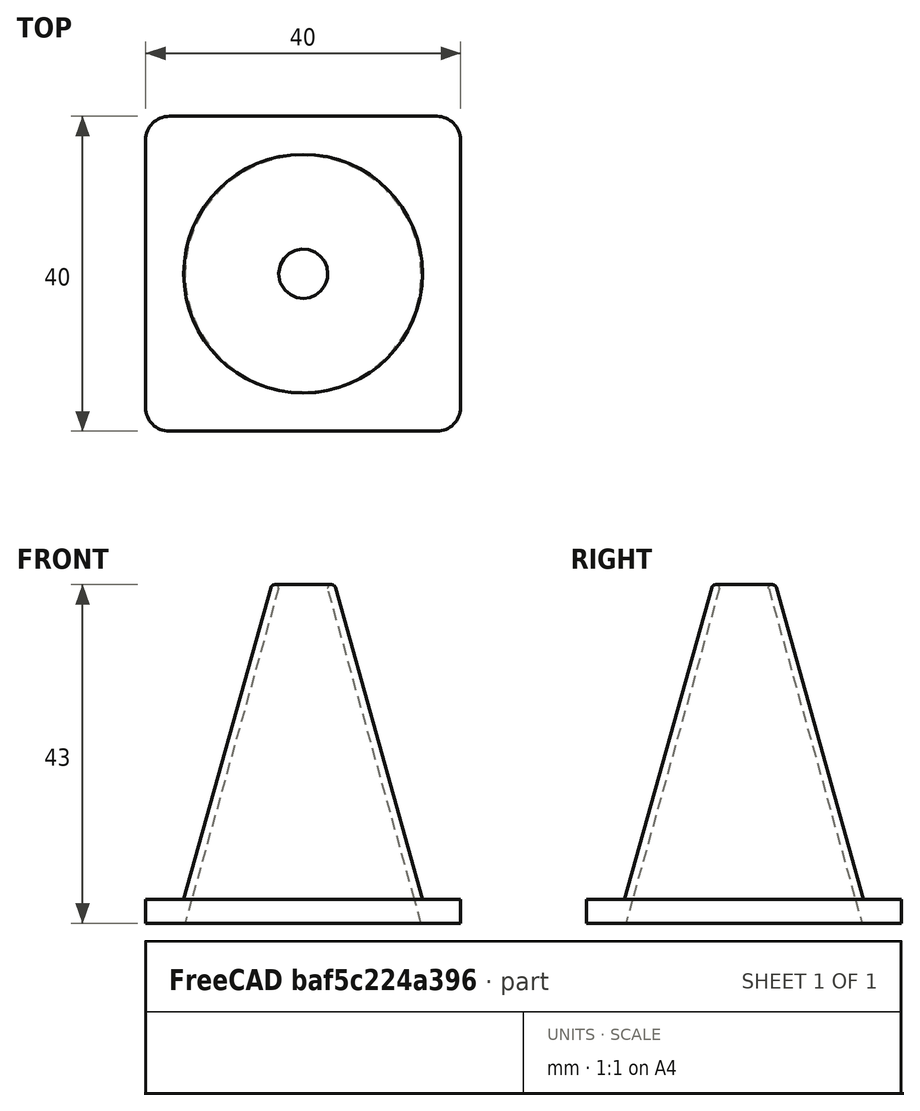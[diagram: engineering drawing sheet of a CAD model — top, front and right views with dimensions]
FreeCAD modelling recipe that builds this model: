
FCSTD DOCUMENT  (FreeCAD 0.18.4R)
Label: tutorial_freecad_ex14_c
License: All rights reserved
LicenseURL: http://en.wikipedia.org/wiki/All_rights_reserved
objects: Part::Fillet×3, Part::Cone×2, Part::Cut×2, Part::Box×1, Part::MultiFuse×1
note: 9 computed .brp shape members not serialized (recipe doc carries the construction recipe); baked Part::Feature solids carry a one-line shape summary decoded from their .brp

FEATURE [Part::Cone] Cone  label="cono_exterior"
  Angle = 360
  AttacherType = Attacher::AttachEngine3D
  Height = 43
  Placement = pos=(20,20,0) rot=(0,0,1;0rad)
  Radius1 = 16
  Radius2 = 4
FEATURE [Part::Cone] Cone001  label="cono_interior"
  Angle = 360
  AttacherType = Attacher::AttachEngine3D
  Height = 43
  Placement = pos=(20,20,0) rot=(0,0,1;0rad)
  Radius1 = 15
  Radius2 = 3
FEATURE [Part::Box] Box  label="base"
  AttacherType = Attacher::AttachEngine3D
  Height = 3
  Length = 40
  Width = 40
FEATURE [Part::Fillet] Fillet  label="base_redondeada"
  Base = -> Box
  Edges = 4 edges r=3: [Edge1,Edge3,Edge5,Edge7]
FEATURE [Part::Cut] Cut  label="cono_sin_base"
  Base = -> Cone
  Refine = true
  Tool = -> Cone001
FEATURE [Part::Fillet] Fillet001
  Base = -> Cut
  Edges = 1 edges r=0.4: [Edge4]
FEATURE [Part::Fillet] Fillet002  label="cono_redondeado"
  Base = -> Fillet001
  Edges = 1 edges r=0.5: [Edge2]
FEATURE [Part::Cut] Cut001  label="base_redondeada_menos_cono_interior"
  Base = -> Fillet
  Refine = true
  Tool = -> Cone001
FEATURE [Part::MultiFuse] Fusion  label="cono_final"
  Refine = true
  Shapes = -> [Cut001,Fillet002]
